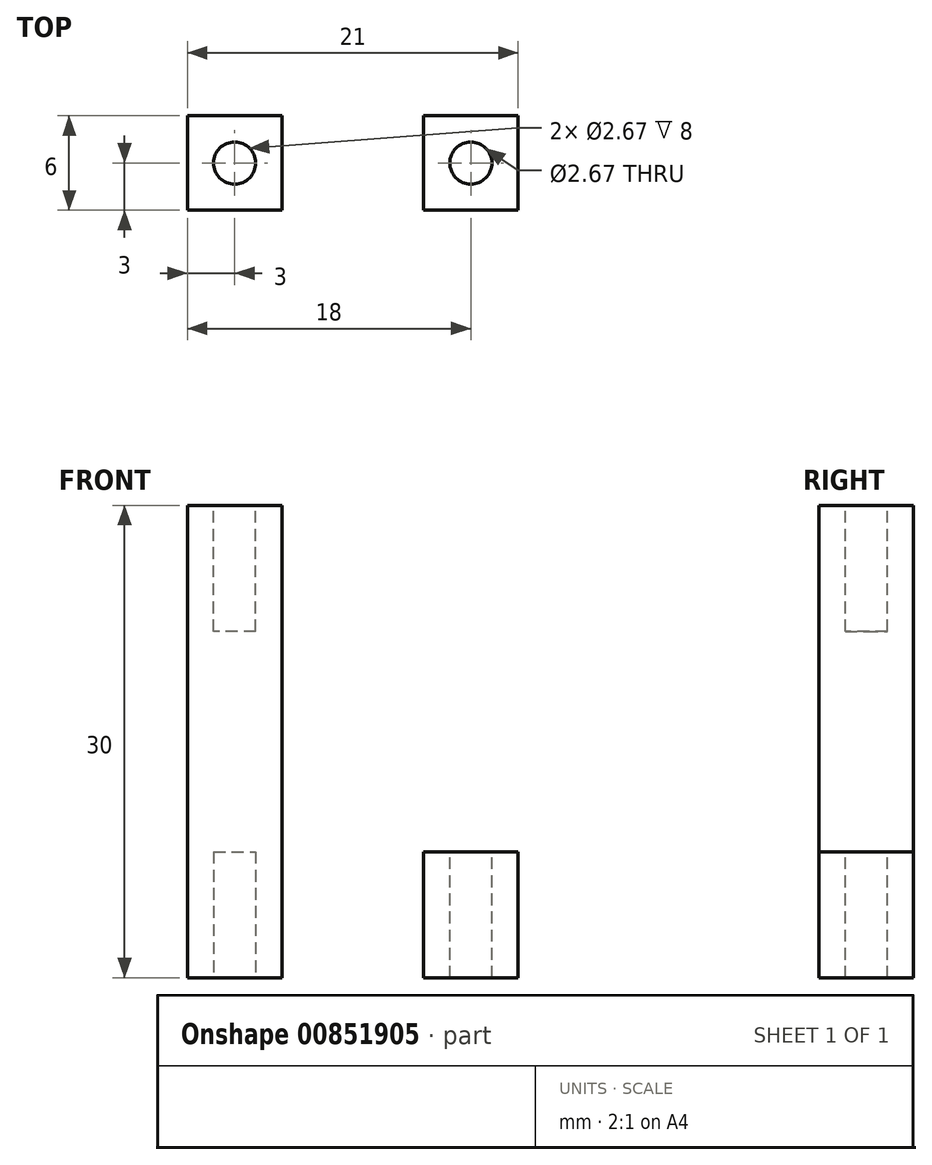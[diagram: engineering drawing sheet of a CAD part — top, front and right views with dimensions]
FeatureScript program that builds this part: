
annotation { "Feature Type Name" : "Feature", "Feature Type Description" : "" }
export const myFeature = defineFeature(function(context is Context, id is Id, definition is map)
    precondition{}
    {
        {
            var Q0;
            Q0=qCreatedBy(makeId("Top.planeOp"),FACE);
            var sketch = newSketch(context, id + "F0", { "sketchPlane" : qUnion([Q0])});
            skLineSegment(sketch, "E0.bottom", {"start": v(3, 3) * mm, "end": v(-3, 3) * mm});
            skLineSegment(sketch, "E0.top", {"start": v(3, -3) * mm, "end": v(-3, -3) * mm});
            skLineSegment(sketch, "E0.left", {"start": v(3, 3) * mm, "end": v(3, -3) * mm});
            skLineSegment(sketch, "E0.right", {"start": v(-3, 3) * mm, "end": v(-3, -3) * mm});
            skPoint(sketch, "E0.middle", {"position": v(0, 0) * mm});
            skLineSegment(sketch, "E1.bottom", {"start": v(12, 3) * mm, "end": v(18, 3) * mm});
            skLineSegment(sketch, "E1.top", {"start": v(12, -3) * mm, "end": v(18, -3) * mm});
            skLineSegment(sketch, "E1.left", {"start": v(12, 3) * mm, "end": v(12, -3) * mm});
            skLineSegment(sketch, "E1.right", {"start": v(18, 3) * mm, "end": v(18, -3) * mm});
            skPoint(sketch, "E1.middle", {"position": v(15, 0) * mm});
            skSolve(sketch);
        }
        {
            var Q0;
            Q0=makeQuery(id+"F0.imprint","IMPRINT",FACE,{"disambiguationData":[TD([[makeQuery(id+"F0.imprint","IMPRINT",EDGE,{"derivedFrom":sQuery(id+"F0.wireOp",EDGE,"E0.bottom")}),1.0]])]});
            extrude(context, id + "F1", {"entities" : qUnion([Q0]), "depth" : 30 * mm, "offsetDistance" : 25 * mm});
        }
        {
            var Q0;
            Q0=makeQuery(id+"F1.opExtrude","CAP_FACE",FACE,{"disambiguationData":[OSD([sQuery(id+"F0.wireOp",EDGE,"E0.bottom"),sQuery(id+"F0.wireOp",EDGE,"E0.top"),sQuery(id+"F0.wireOp",EDGE,"E0.left"),sQuery(id+"F0.wireOp",EDGE,"E0.right")])],"isStart":false});
            var sketch = newSketch(context, id + "F2", { "sketchPlane" : qUnion([Q0])});
            skCircle(sketch, "E2", {"center": v(0, 0) * mm, "radius": 1.33 * mm});
            skSolve(sketch);
        }
        {
            var Q0;
            Q0=makeQuery(id+"F2.imprint","IMPRINT",FACE,{"disambiguationData":[TD([[makeQuery(id+"F2.imprint","IMPRINT",EDGE,{"derivedFrom":sQuery(id+"F2.wireOp",EDGE,"E2")}),1.0]])]});
            extrude(context, id + "F3", {"entities" : qUnion([Q0]), "operationType" : NewBodyOperationType.REMOVE, "oppositeDirection" : true, "depth" : 8 * mm, "offsetDistance" : 25 * mm});
        }
        {
            var Q0;
            Q0=makeQuery(id+"F1.opExtrude","CAP_FACE",FACE,{"disambiguationData":[OSD([sQuery(id+"F0.wireOp",EDGE,"E0.bottom"),sQuery(id+"F0.wireOp",EDGE,"E0.top"),sQuery(id+"F0.wireOp",EDGE,"E0.left"),sQuery(id+"F0.wireOp",EDGE,"E0.right")])],"isStart":true});
            var sketch = newSketch(context, id + "F4", { "sketchPlane" : qUnion([Q0])});
            skCircle(sketch, "E3", {"center": v(0, 0) * mm, "radius": 1.33 * mm});
            skSolve(sketch);
        }
        {
            var Q0;
            Q0=makeQuery(id+"F4.imprint","IMPRINT",FACE,{"disambiguationData":[TD([[makeQuery(id+"F4.imprint","IMPRINT",EDGE,{"derivedFrom":sQuery(id+"F4.wireOp",EDGE,"E3")}),1.0]])]});
            extrude(context, id + "F5", {"entities" : qUnion([Q0]), "operationType" : NewBodyOperationType.REMOVE, "oppositeDirection" : true, "depth" : 8 * mm, "offsetDistance" : 25 * mm});
        }
        {
            var Q0;
            Q0=makeQuery(id+"F0.imprint","IMPRINT",FACE,{"disambiguationData":[TD([[makeQuery(id+"F0.imprint","IMPRINT",EDGE,{"derivedFrom":sQuery(id+"F0.wireOp",EDGE,"E1.bottom")}),-1.0]])]});
            extrude(context, id + "F6", {"entities" : qUnion([Q0]), "depth" : 8 * mm, "offsetDistance" : 25 * mm});
        }
        {
            var Q0;
            Q0=makeQuery(id+"F6.opExtrude","CAP_FACE",FACE,{"disambiguationData":[OSD([sQuery(id+"F0.wireOp",EDGE,"E1.bottom"),sQuery(id+"F0.wireOp",EDGE,"E1.top"),sQuery(id+"F0.wireOp",EDGE,"E1.left"),sQuery(id+"F0.wireOp",EDGE,"E1.right")])],"isStart":false});
            var sketch = newSketch(context, id + "F7", { "sketchPlane" : qUnion([Q0])});
            skCircle(sketch, "E4", {"center": v(15, 0) * mm, "radius": 1.33 * mm});
            skSolve(sketch);
        }
        {
            var Q0;
            Q0=makeQuery(id+"F6.opExtrude","CAP_FACE",FACE,{"disambiguationData":[OSD([sQuery(id+"F0.wireOp",EDGE,"E1.bottom"),sQuery(id+"F0.wireOp",EDGE,"E1.top"),sQuery(id+"F0.wireOp",EDGE,"E1.left"),sQuery(id+"F0.wireOp",EDGE,"E1.right")])],"isStart":true});
            var sketch = newSketch(context, id + "F8", { "sketchPlane" : qUnion([Q0])});
            skCircle(sketch, "E5", {"center": v(15, 0) * mm, "radius": 1.33 * mm});
            skPoint(sketch, "E5.centerSnap0", {"position": v(15, 3) * mm});
            skPoint(sketch, "E5.centerSnap1", {"position": v(12, 0) * mm});
            skSolve(sketch);
        }
        {
            var Q0;
            Q0=makeQuery(id+"F7.imprint","IMPRINT",FACE,{"disambiguationData":[TD([[makeQuery(id+"F7.imprint","IMPRINT",EDGE,{"derivedFrom":sQuery(id+"F7.wireOp",EDGE,"E4")}),1.0]])]});
            var Q1;
            Q1=makeQuery(id+"F8.imprint","IMPRINT",FACE,{"disambiguationData":[TD([[makeQuery(id+"F8.imprint","IMPRINT",EDGE,{"derivedFrom":sQuery(id+"F8.wireOp",EDGE,"E5")}),1.0]])]});
            extrude(context, id + "F9", {"entities" : qUnion([Q0, Q1]), "operationType" : NewBodyOperationType.REMOVE, "endBound" : BoundingType.THROUGH_ALL, "oppositeDirection" : true, "depth" : 2.8 * mm, "offsetDistance" : 25 * mm});
        }
    });
